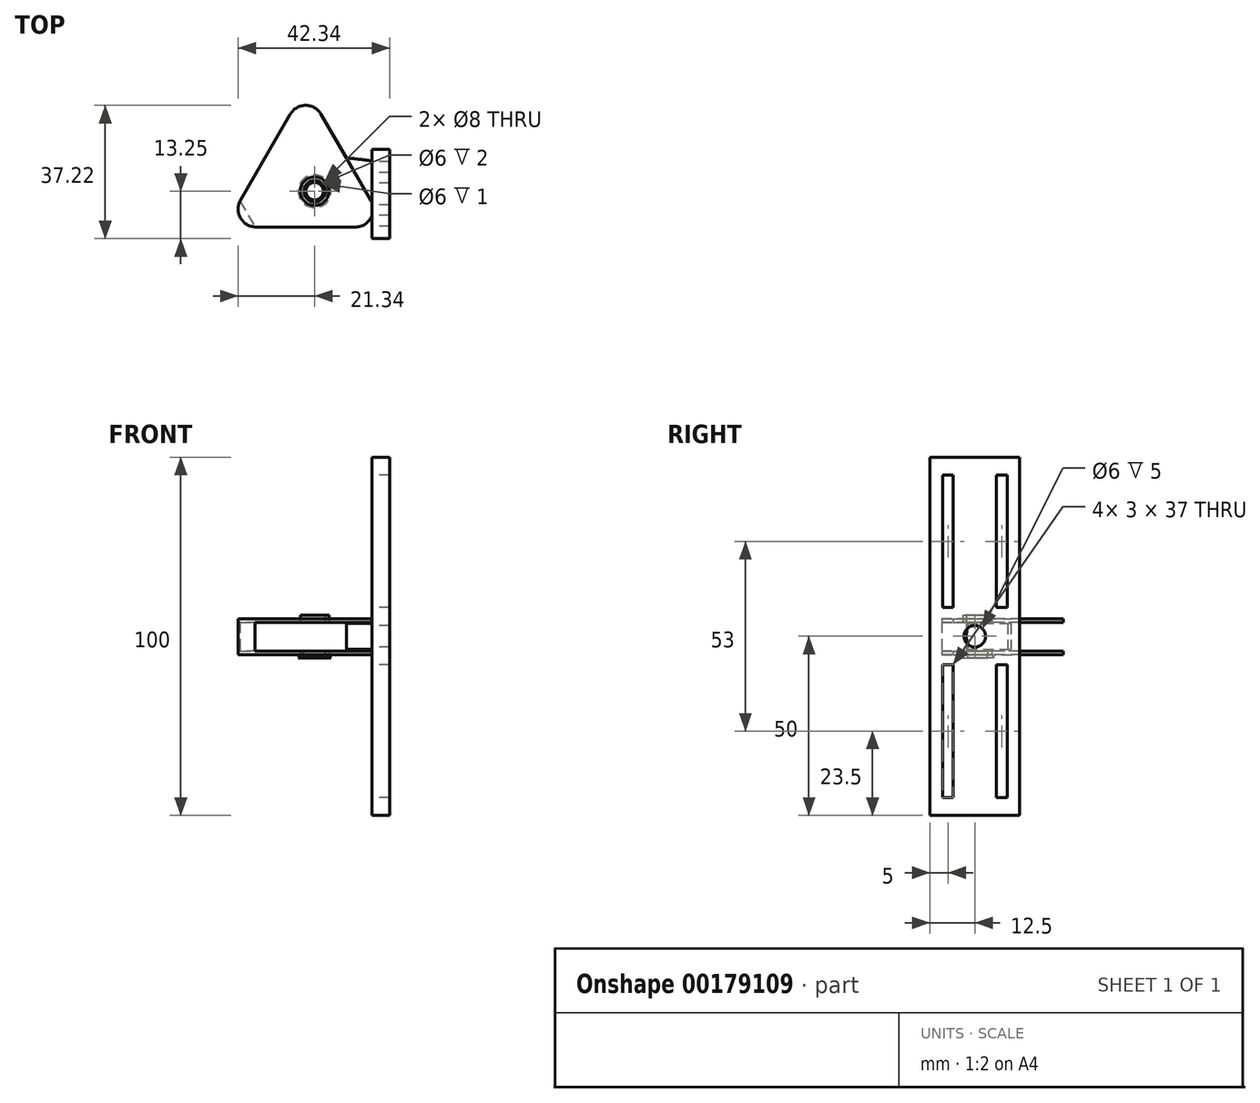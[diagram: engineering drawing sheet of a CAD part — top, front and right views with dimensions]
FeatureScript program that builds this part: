
annotation { "Feature Type Name" : "Feature", "Feature Type Description" : "" }
export const myFeature = defineFeature(function(context is Context, id is Id, definition is map)
    precondition{}
    {
        {
            var Q0;
            Q0=qCreatedBy(makeId("Top.planeOp"),FACE);
            var sketch = newSketch(context, id + "F0", { "sketchPlane" : qUnion([Q0])});
            skLineSegment(sketch, "E0", {"start": v(-4.33, 7.5) * mm, "end": v(-18.17, 31.47) * mm});
            skLineSegment(sketch, "E1", {"start": v(-26.83, 31.47) * mm, "end": v(-40.67, 7.5) * mm});
            skLineSegment(sketch, "E2", {"start": v(-36.34, 0) * mm, "end": v(-8.66, 0) * mm});
            skLineSegment(sketch, "E3", {"start": v(-20, 0) * mm, "end": v(-20, 10) * mm, "construction": true});
            skCircle(sketch, "E4", {"center": v(-20, 10) * mm, "radius": 4 * mm});
            skPoint(sketch, "E5.visualSharp", {"position": v(0, 0) * mm});
            skArc(sketch, "E5.filletArc", {"start": v(-8.66, 0) * mm, "mid": v(-4.33, 2.5) * mm, "end": v(-4.33, 7.5) * mm});
            skPoint(sketch, "E6.visualSharp", {"position": v(-45, 0) * mm});
            skArc(sketch, "E6.filletArc", {"start": v(-40.67, 7.5) * mm, "mid": v(-40.67, 2.5) * mm, "end": v(-36.34, 0) * mm});
            skPoint(sketch, "E7.visualSharp", {"position": v(-22.5, 38.97) * mm});
            skArc(sketch, "E7.filletArc", {"start": v(-18.17, 31.47) * mm, "mid": v(-22.5, 33.97) * mm, "end": v(-26.83, 31.47) * mm});
            skSolve(sketch);
        }
        {
            var Q0;
            Q0=qCreatedBy(makeId("Top.planeOp"),FACE);
            var sketch = newSketch(context, id + "F1", { "sketchPlane" : qUnion([Q0])});
            skCircle(sketch, "E8", {"center": v(-20, 10) * mm, "radius": 4 * mm});
            skLineSegment(sketch, "E9.bottom", {"start": v(-30, 0) * mm, "end": v(0, 0) * mm});
            skLineSegment(sketch, "E9.top", {"start": v(-25, 25) * mm, "end": v(0, 25) * mm});
            skLineSegment(sketch, "E9.left", {"start": v(-30, 0) * mm, "end": v(-30, 20) * mm});
            skLineSegment(sketch, "E9.right", {"start": v(0, 0) * mm, "end": v(0, 25) * mm});
            skCircle(sketch, "E10", {"center": v(-20, 10) * mm, "radius": 3 * mm});
            skLineSegment(sketch, "E11", {"start": v(0, 25) * mm, "end": v(-30, 0) * mm, "construction": true});
            skPoint(sketch, "E12.visualSharp", {"position": v(-30, 25) * mm});
            skArc(sketch, "E12.filletArc", {"start": v(-25, 25) * mm, "mid": v(-28.54, 23.54) * mm, "end": v(-30, 20) * mm});
            skPoint(sketch, "E13.visualSharp", {"position": v(0, 0) * mm});
            skLineSegment(sketch, "E14", {"start": v(-4, 0) * mm, "end": v(-4, 18.5) * mm});
            skLineSegment(sketch, "E15", {"start": v(-4, 18.5) * mm, "end": v(0, 18.5) * mm});
            skLineSegment(sketch, "E16", {"start": v(-4, 18.5) * mm, "end": v(-9.42, 25) * mm});
            skArc(sketch, "E17", {"start": v(-4, 18.5) * mm, "mid": v(-14, 23.34) * mm, "end": v(-25, 25) * mm});
            skFitSpline(sketch, "E18", {"points": [v(-4, 18.5) * mm, v(-30, 15.65) * mm], "startDerivative": vector(-28.14, 3.2) * mm, "endDerivative": vector(-29, -16.2) * mm});
            skSolve(sketch);
        }
        {
            var Q0;
            {var subQ0=sQuery(id+"F0.wireOp",EDGE,"E1");Q0=makeQuery(id+"F0.imprint","IMPRINT",FACE,{"disambiguationData":[TD([[makeQuery(id+"F0.imprint","IMPRINT",EDGE,{"derivedFrom":subQ0}),1.0]])]});}
            extrude(context, id + "F2", {"entities" : qUnion([Q0]), "depth" : 10 * mm});
        }
        {
            var Q0;
            Q0=makeQuery(id+"F1.imprint","IMPRINT",FACE,{"disambiguationData":[TD([[makeQuery(id+"F1.imprint","IMPRINT",EDGE,{"derivedFrom":sQuery(id+"F1.wireOp",EDGE,"E8")}),1.0]])]});
            extrude(context, id + "F3", {"entities" : qUnion([Q0]), "oppositeDirection" : true, "depth" : 1 * mm, "hasDraft" : true, "draftAngle" : 30 * degree, "hasSecondDirection" : true, "secondDirectionOppositeDirection" : false, "secondDirectionDepth" : 11 * mm});
        }
        {
            var Q0;
            Q0=makeQuery(id+"F1.imprint","IMPRINT",FACE,{"disambiguationData":[TD([[makeQuery(id+"F1.imprint","IMPRINT",EDGE,{"derivedFrom":sQuery(id+"F1.wireOp",EDGE,"E8")}),-1.0]])]});
            extrude(context, id + "F4", {"entities" : qUnion([Q0]), "depth" : 8.7 * mm, "hasSecondDirection" : true, "secondDirectionOppositeDirection" : false, "secondDirectionDepth" : 1.5 * mm});
        }
        {
            var Q0;
            Q0=makeQuery(id+"FArU3wWUGcGf4vr_3.opExtrude","CAP_EDGE",EDGE,{"disambiguationData":[OSD([sQuery(id+"F1.wireOp",EDGE,"E14")])],"isStart":false});
            var Q1;
            {var subQ0=sQuery(id+"F1.wireOp",EDGE,"E14");var subQ1=sQuery(id+"F1.wireOp",EDGE,"E18");var subQ2=sQuery(id+"F1.wireOp",EDGE,"E9.bottom");var subQ3=sQuery(id+"F1.wireOp",EDGE,"E15");Q1=makeQuery(id+"FArU3wWUGcGf4vr_3.boolean.opBoolean","SPLIT",EDGE,{"disambiguationData":[TD([makeQuery(id+"FArU3wWUGcGf4vr_3.opExtrude","CAP_FACE",FACE,{"disambiguationData":[OSD([subQ2,sQuery(id+"F1.wireOp",EDGE,"E9.right"),subQ0,subQ3])],"isStart":true})])],"derivedFrom":makeQuery(id+"FArU3wWUGcGf4vr_3.opExtrude","SWEPT_EDGE",EDGE,{"disambiguationData":[OSD([subQ0,subQ3,sQuery(id+"F1.wireOp",EDGE,"E16"),sQuery(id+"F1.wireOp",EDGE,"E17"),subQ1])]})});}
            var Q2;
            Q2=makeQuery(id+"FArU3wWUGcGf4vr_3.opExtrude","CAP_EDGE",EDGE,{"disambiguationData":[OSD([sQuery(id+"F1.wireOp",EDGE,"E14")])],"isStart":true});
            var Q3;
            {var subQ0=sQuery(id+"F1.wireOp",EDGE,"E14");var subQ1=sQuery(id+"F1.wireOp",EDGE,"E15");var subQ2=sQuery(id+"F1.wireOp",EDGE,"E9.bottom");var subQ3=sQuery(id+"F1.wireOp",EDGE,"E18");Q3=makeQuery(id+"FArU3wWUGcGf4vr_3.boolean.opBoolean","SPLIT",EDGE,{"disambiguationData":[TD([makeQuery(id+"FArU3wWUGcGf4vr_3.opExtrude","CAP_FACE",FACE,{"disambiguationData":[OSD([subQ2,sQuery(id+"F1.wireOp",EDGE,"E9.right"),subQ0,subQ1])],"isStart":false})])],"derivedFrom":makeQuery(id+"FArU3wWUGcGf4vr_3.opExtrude","SWEPT_EDGE",EDGE,{"disambiguationData":[OSD([subQ0,subQ1,sQuery(id+"F1.wireOp",EDGE,"E16"),sQuery(id+"F1.wireOp",EDGE,"E17"),subQ3])]})});}
            var Q4;
            Q4=makeQuery(id+"F4.opExtrude","CAP_EDGE",EDGE,{"disambiguationData":[OSD([sQuery(id+"F1.wireOp",EDGE,"E9.left")])],"isStart":true});
            var Q5;
            Q5=makeQuery(id+"F4.opExtrude","CAP_EDGE",EDGE,{"disambiguationData":[OSD([sQuery(id+"F1.wireOp",EDGE,"E9.left")])],"isStart":false});
            fillet(context, id + "F5", {"entities" : qUnion([Q0, Q1, Q2, Q3, Q4, Q5]), "radius" : 1 * mm, "tangentPropagation" : true, "allowEdgeOverflow" : false});
        }
        {
            var Q0;
            Q0=makeQuery(id+"F2.opExtrude","SWEPT_FACE",FACE,{"disambiguationData":[OSD([sQuery(id+"F0.wireOp",EDGE,"E0")])]});
            var sketch = newSketch(context, id + "F6", { "sketchPlane" : qUnion([Q0])});
            skLineSegment(sketch, "E19", {"start": v(8.66, 5) * mm, "end": v(36.34, 5) * mm, "construction": true});
            skPoint(sketch, "E20", {"position": v(36.34, 9) * mm});
            skPoint(sketch, "E21.MirrorP", {"position": v(36.34, 1) * mm});
            skLineSegment(sketch, "E22.bottom", {"start": v(36.34, 9) * mm, "end": v(8.66, 9) * mm});
            skLineSegment(sketch, "E22.top", {"start": v(36.34, 1) * mm, "end": v(8.66, 1) * mm});
            skLineSegment(sketch, "E22.left", {"start": v(36.34, 9) * mm, "end": v(36.34, 1) * mm});
            skLineSegment(sketch, "E22.right", {"start": v(8.66, 9) * mm, "end": v(8.66, 1) * mm});
            skLineSegment(sketch, "E23.bottom", {"start": v(46.34, 9) * mm, "end": v(-1.34, 9) * mm});
            skLineSegment(sketch, "E23.top", {"start": v(46.34, 1) * mm, "end": v(-1.34, 1) * mm});
            skLineSegment(sketch, "E23.left", {"start": v(46.34, 9) * mm, "end": v(46.34, 1) * mm});
            skLineSegment(sketch, "E23.right", {"start": v(-1.34, 9) * mm, "end": v(-1.34, 1) * mm});
            skLineSegment(sketch, "E24", {"start": v(28.54, 10) * mm, "end": v(33.05, 10) * mm});
            skLineSegment(sketch, "E25", {"start": v(25.79, 0) * mm, "end": v(30.89, 0) * mm});
            skSolve(sketch);
        }
        {
            var Q0;
            {var subQ0=sQuery(id+"F6.wireOp",EDGE,"E22.right");Q0=makeQuery(id+"F6.imprint","IMPRINT",FACE,{"disambiguationData":[TD([[makeQuery(id+"F6.imprint","IMPRINT",EDGE,{"derivedFrom":subQ0}),-1.0]])]});}
            var Q1;
            {var subQ0=sQuery(id+"F6.wireOp",EDGE,"E22.left");Q1=makeQuery(id+"F6.imprint","IMPRINT",FACE,{"disambiguationData":[TD([[makeQuery(id+"F6.imprint","IMPRINT",EDGE,{"derivedFrom":subQ0}),-1.0]])]});}
            var Q2;
            {var subQ0=sQuery(id+"F6.wireOp",EDGE,"E22.left");Q2=makeQuery(id+"F6.imprint","IMPRINT",FACE,{"disambiguationData":[TD([[makeQuery(id+"F6.imprint","IMPRINT",EDGE,{"derivedFrom":subQ0}),1.0]])]});}
            extrude(context, id + "F7", {"entities" : qUnion([Q0, Q1, Q2]), "operationType" : NewBodyOperationType.REMOVE, "oppositeDirection" : true, "depth" : 31.7 * mm});
        }
        {
            var Q0;
            Q0=makeQuery(id+"F4.opExtrude","SWEPT_FACE",FACE,{"disambiguationData":[OSD([sQuery(id+"F1.wireOp",EDGE,"E14")])]});
            var sketch = newSketch(context, id + "F8", { "sketchPlane" : qUnion([Q0])});
            skPoint(sketch, "E26", {"position": v(9.25, 5.1) * mm});
            skPoint(sketch, "E26.positionSnap0", {"position": v(9.25, 8.7) * mm});
            skPoint(sketch, "E26.positionSnap1", {"position": v(18.5, 5.1) * mm});
            skLineSegment(sketch, "E27", {"start": v(18.5, 5.1) * mm, "end": v(0, 5.1) * mm, "construction": true});
            skCircle(sketch, "E28", {"center": v(9.25, 5.1) * mm, "radius": 3 * mm});
            skLineSegment(sketch, "E29.bottom", {"start": v(21.75, -44.9) * mm, "end": v(-3.25, -44.9) * mm});
            skLineSegment(sketch, "E29.top", {"start": v(21.75, 55.1) * mm, "end": v(-3.25, 55.1) * mm});
            skLineSegment(sketch, "E29.left", {"start": v(21.75, -44.9) * mm, "end": v(21.75, 55.1) * mm});
            skLineSegment(sketch, "E29.right", {"start": v(-3.25, -44.9) * mm, "end": v(-3.25, 55.1) * mm});
            skLineSegment(sketch, "E30", {"start": v(16.75, 50.1) * mm, "end": v(16.75, 13.1) * mm, "construction": true});
            skLineSegment(sketch, "E31", {"start": v(1.75, 50.1) * mm, "end": v(1.75, 13.1) * mm, "construction": true});
            skLineSegment(sketch, "E32.0.left", {"start": v(18.25, 50.1) * mm, "end": v(18.25, 13.1) * mm});
            skLineSegment(sketch, "E32.0.right", {"start": v(15.25, 50.1) * mm, "end": v(15.25, 13.1) * mm});
            skLineSegment(sketch, "E33.0.left", {"start": v(3.25, 50.1) * mm, "end": v(3.25, 13.1) * mm});
            skLineSegment(sketch, "E33.0.right", {"start": v(0.25, 50.1) * mm, "end": v(0.25, 13.1) * mm});
            skLineSegment(sketch, "E34", {"start": v(18.25, 50.1) * mm, "end": v(15.25, 50.1) * mm});
            skLineSegment(sketch, "E35", {"start": v(15.25, 13.1) * mm, "end": v(18.25, 13.1) * mm});
            skLineSegment(sketch, "E36", {"start": v(3.25, 50.1) * mm, "end": v(0.25, 50.1) * mm});
            skLineSegment(sketch, "E37", {"start": v(0.25, 13.1) * mm, "end": v(3.25, 13.1) * mm});
            skLineSegment(sketch, "E38.MirrorCS", {"start": v(15.25, -2.9) * mm, "end": v(18.25, -2.9) * mm});
            skLineSegment(sketch, "E39.MirrorCS", {"start": v(16.75, -39.9) * mm, "end": v(16.75, -2.9) * mm, "construction": true});
            skLineSegment(sketch, "E40.MirrorCS", {"start": v(18.25, -39.9) * mm, "end": v(18.25, -2.9) * mm});
            skLineSegment(sketch, "E41.MirrorCS", {"start": v(15.25, -39.9) * mm, "end": v(15.25, -2.9) * mm});
            skLineSegment(sketch, "E42.MirrorCS", {"start": v(18.25, -39.9) * mm, "end": v(15.25, -39.9) * mm});
            skLineSegment(sketch, "E43.MirrorCS", {"start": v(0.25, -2.9) * mm, "end": v(3.25, -2.9) * mm});
            skLineSegment(sketch, "E44.MirrorCS", {"start": v(1.75, -39.9) * mm, "end": v(1.75, -2.9) * mm, "construction": true});
            skLineSegment(sketch, "E45.MirrorCS", {"start": v(3.25, -39.9) * mm, "end": v(3.25, -2.9) * mm});
            skLineSegment(sketch, "E46.MirrorCS", {"start": v(0.25, -39.9) * mm, "end": v(0.25, -2.9) * mm});
            skLineSegment(sketch, "E47.MirrorCS", {"start": v(3.25, -39.9) * mm, "end": v(0.25, -39.9) * mm});
            skSolve(sketch);
        }
        {
            var Q0;
            {var subQ0=sQuery(id+"F8.wireOp",EDGE,"Gr41VuB3-8Q0Q-Amji-nHSh-x4tqxf1g2mUt.top");Q0=makeQuery(id+"F8.imprint","IMPRINT",FACE,{"disambiguationData":[TD([[makeQuery(id+"F8.imprint","IMPRINT",EDGE,{"derivedFrom":subQ0}),1.0]])]});}
            var Q1;
            {var subQ0=sQuery(id+"F8.wireOp",EDGE,"Gr41VuB3-8Q0Q-Amji-nHSh-x4tqxf1g2mUt.bottom");Q1=makeQuery(id+"F8.imprint","IMPRINT",FACE,{"disambiguationData":[TD([[makeQuery(id+"F8.imprint","IMPRINT",EDGE,{"derivedFrom":subQ0}),-1.0]])]});}
            var Q2;
            {var subQ1=sQuery(id+"F1.wireOp",EDGE,"E14");var subQ2=makeQuery(id+"F4.opExtrude","CAP_EDGE",EDGE,{"disambiguationData":[OSD([subQ1])],"isStart":true});Q2=makeQuery(id+"F8.imprint","IMPRINT",FACE,{"disambiguationData":[TD([[makeQuery(id+"F8.imprint","IMPRINT",EDGE,{"derivedFrom":subQ2}),1.0]])]});}
            var Q3;
            Q3=makeQuery(id+"F8.imprint","IMPRINT",FACE,{"disambiguationData":[TD([[makeQuery(id+"F8.imprint","IMPRINT",EDGE,{"derivedFrom":sQuery(id+"F8.wireOp",EDGE,"E29.bottom")}),-1.0]])]});
            extrude(context, id + "F9", {"entities" : qUnion([Q0, Q1, Q2, Q3]), "operationType" : NewBodyOperationType.ADD, "depth" : 5 * mm});
        }
    });
